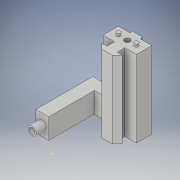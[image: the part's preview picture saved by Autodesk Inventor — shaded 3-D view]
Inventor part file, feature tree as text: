
AUTODESK INVENTOR PART (.ipt)
format: ipt  version: 2018 (Build 220112000, 112)  size: 178,176 bytes
history: native  units: in
note: dims shown in document units (in); Inventor stores cm internally (conversion verified against a paired STEP export)
features: sketch x9, extrude x6, hole x2
ambient origin geometry x8: Origin, YZ Plane, XZ Plane, XY Plane, X Axis, Y Axis, Z Axis, Center Point
bodies: Solid1 (feature_tree)
feature tree (17):
  extrude  "Extrusion1"  Depth=0.3in
  extrude  "Extrusion2"  Depth=0.25in
  extrude  "Extrusion3"  Depth=0.05in
  hole  "Hole1"  [1 undecoded]
  extrude  "Extrusion7"  Depth=0.1in
  extrude  "Extrusion8"  Depth=0.15in
  extrude  "Extrusion9"  Depth=0.05in TaperAngle=0.0deg
  sketch  "Sketch16"  dims[d20=0.15in d21=0.08in]
  hole  "Hole3"  [1 undecoded]
  sketch  "Sketch1"  dims[d0=0.65in d1=0.3in]
  sketch  "Sketch2"  dims[d2=0.1in d3=0.25in]
  sketch  "Sketch3"  dims[d4=0.2in d5=0.05in]
  sketch  "Sketch6"  dims[d6=0.1in d7=0.1in]
  sketch  "Sketch13"  dims[d8=0.1in d9=0.1in]
  sketch  "Sketch14"  dims[d10=1.5in d11=0.0in d12=0.15in]
  sketch  "Sketch15"  dims[d14=0.08in d18=0.05in d19=0.0in]
  sketch  "Sketch17"  dims[d22=0.05in d23=0.0in d24=0.325in d25=0.11in d26=0.11in d27=0.75in d28=0.375in d29=0.25in d30=0.5635in d31=0.45in d32=0.8108in d68=0.22in d69=0.4in d70=0.5in d71=0.0in d72=0.25in d73=0.4in d77=0.89in d78=0.0in d79=0.125in d80=0.16in d81=0.2in d82=0.0in d83=0.11in d84=0.11in d85=0.75in d86=0.375in d87=0.25in d88=0.5635in d89=0.5in d90=0.8108in]
note: 2 required parameter values undecoded (feature->parameter linkage not recoverable at this tier; creation-order binding heuristic only, values carry confidence <= 0.55)
